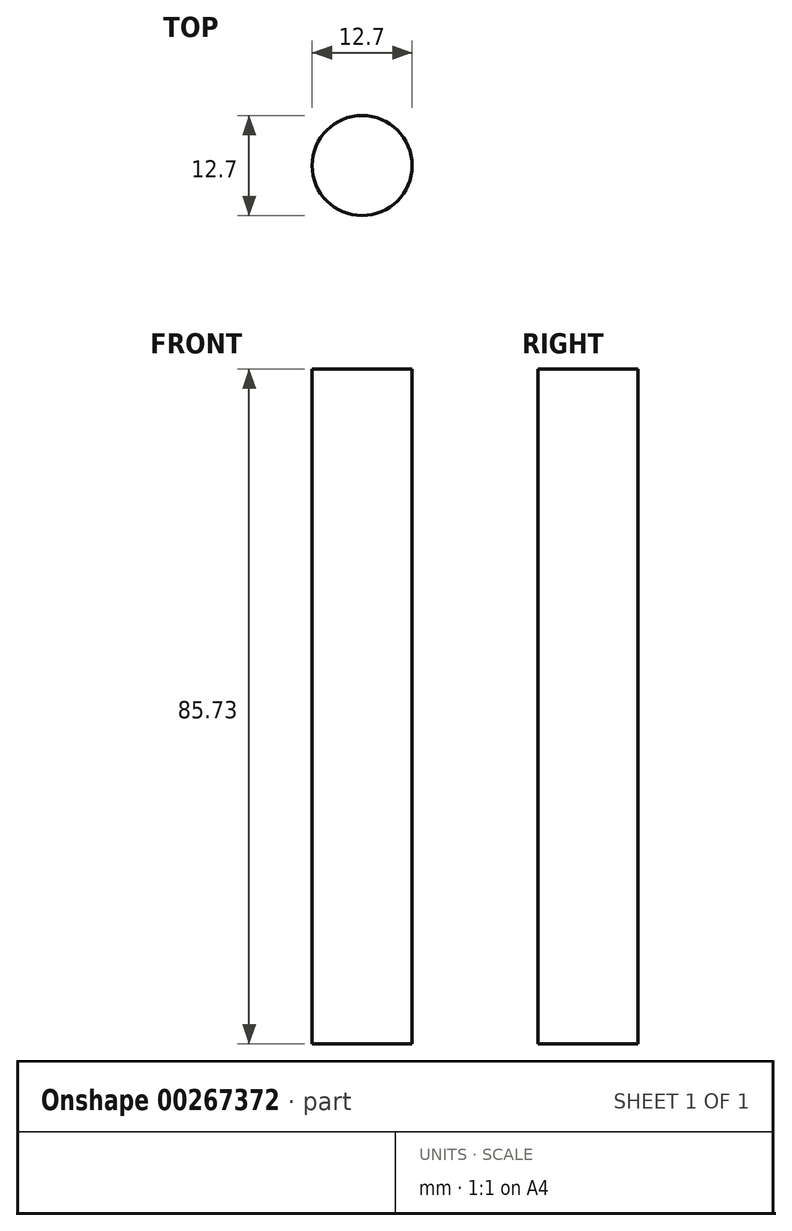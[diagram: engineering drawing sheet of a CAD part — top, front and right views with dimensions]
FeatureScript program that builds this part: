
annotation { "Feature Type Name" : "Feature", "Feature Type Description" : "" }
export const myFeature = defineFeature(function(context is Context, id is Id, definition is map)
    precondition{}
    {
        {
            var Q0;
            Q0=qCreatedBy(makeId("Top.planeOp"),FACE);
            var sketch = newSketch(context, id + "F0", { "sketchPlane" : qUnion([Q0])});
            skCircle(sketch, "E0", {"center": v(0, 0) * mm, "radius": 6.35 * mm});
            skSolve(sketch);
        }
        {
            var Q0;
            Q0=makeQuery(id+"F0.imprint","IMPRINT",FACE,{"disambiguationData":[TD([[makeQuery(id+"F0.imprint","IMPRINT",EDGE,{"derivedFrom":sQuery(id+"F0.wireOp",EDGE,"E0")}),1.0]])]});
            extrude(context, id + "F1", {"entities" : qUnion([Q0]), "depth" : 85.72 * mm});
        }
    });
